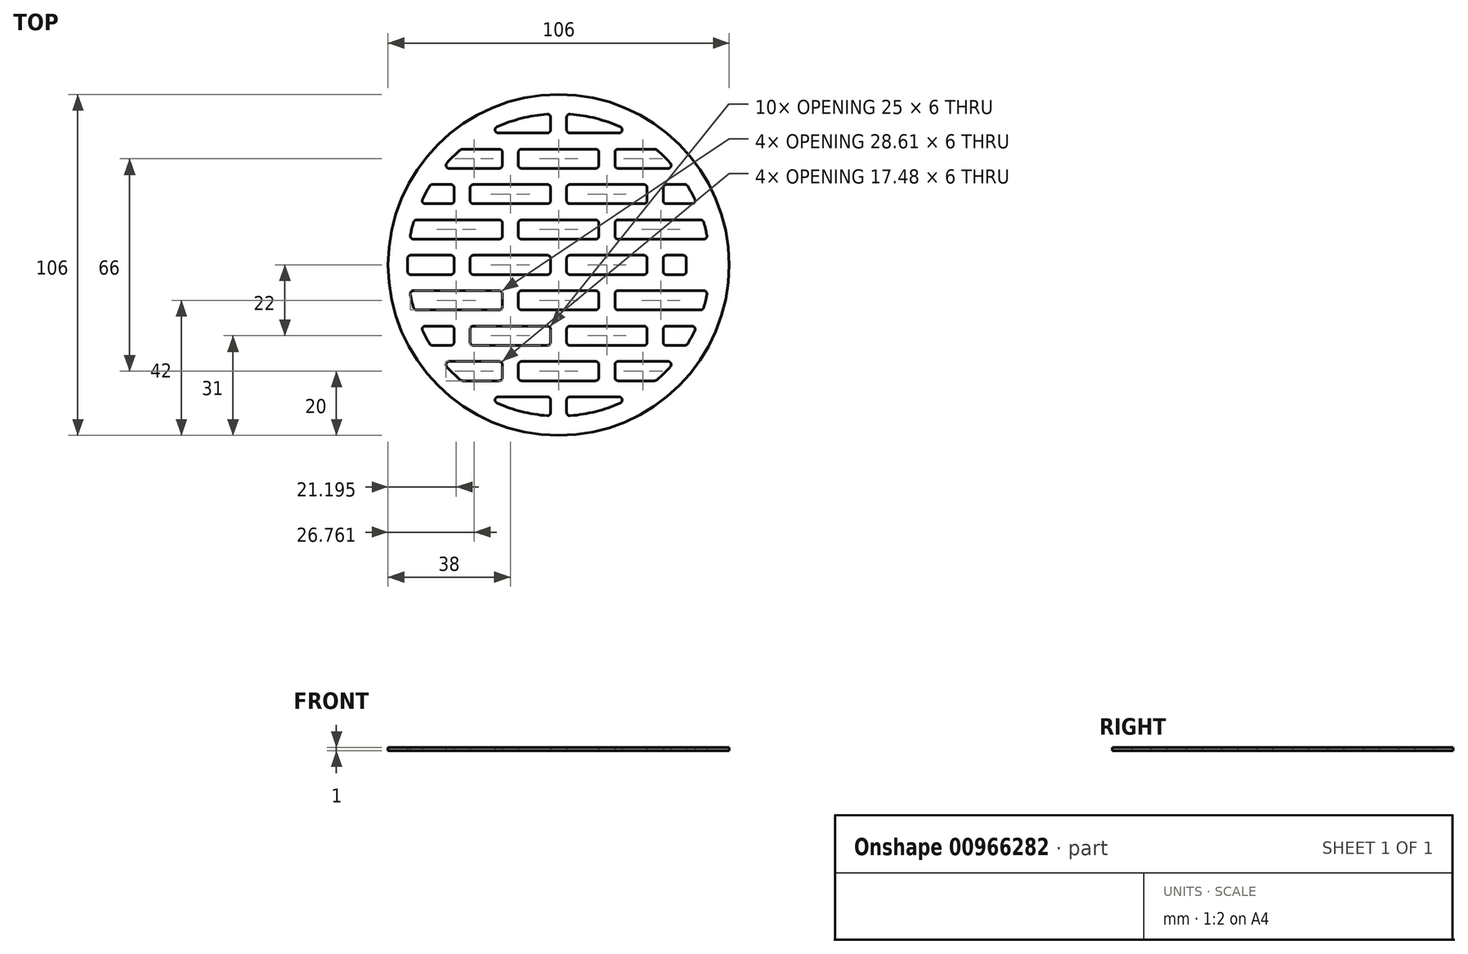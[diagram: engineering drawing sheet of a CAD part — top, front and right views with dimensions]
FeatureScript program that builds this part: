
annotation { "Feature Type Name" : "Feature", "Feature Type Description" : "" }
export const myFeature = defineFeature(function(context is Context, id is Id, definition is map)
    precondition{}
    {
        {
            var Q0;
            Q0=qCreatedBy(makeId("Top.planeOp"),FACE);
            var sketch = newSketch(context, id + "F0", { "sketchPlane" : qUnion([Q0])});
            skCircle(sketch, "E0", {"center": v(0, 0) * mm, "radius": 53 * mm});
            skArc(sketch, "E1", {"start": v(22.98, 41) * mm, "mid": v(13.08, 45.14) * mm, "end": v(2.5, 46.93) * mm});
            skLineSegment(sketch, "E2", {"start": v(-47, 0) * mm, "end": v(39.7, 0) * mm, "construction": true});
            skLineSegment(sketch, "E3.0", {"start": v(-46.9, -3) * mm, "end": v(-32.5, -3) * mm});
            skLineSegment(sketch, "E4.0", {"start": v(-46.9, 3) * mm, "end": v(-32.5, 3) * mm});
            skLineSegment(sketch, "E5", {"start": v(0, 47) * mm, "end": v(0, -47) * mm, "construction": true});
            skLineSegment(sketch, "E6.0", {"start": v(2.5, 46.93) * mm, "end": v(2.5, 41) * mm});
            skLineSegment(sketch, "E7.0", {"start": v(-2.5, 46.93) * mm, "end": v(-2.5, 41) * mm});
            skLineSegment(sketch, "E8.0.1.0", {"start": v(-46.9, 8) * mm, "end": v(-17.5, 8) * mm});
            skLineSegment(sketch, "E8.0.1.1", {"start": v(-44.87, 14) * mm, "end": v(-17.5, 14) * mm});
            skLineSegment(sketch, "E8.0.2.0", {"start": v(-42.99, 19) * mm, "end": v(-32.5, 19) * mm});
            skLineSegment(sketch, "E8.0.2.1", {"start": v(-39.8, 25) * mm, "end": v(-32.5, 25) * mm});
            skLineSegment(sketch, "E8.0.3.0", {"start": v(-36.18, 30) * mm, "end": v(-17.5, 30) * mm});
            skLineSegment(sketch, "E8.direction1", {"start": v(-46.9, -3) * mm, "end": v(-32.5, -3) * mm, "construction": true});
            skLineSegment(sketch, "E8.direction2", {"start": v(-46.9, -3) * mm, "end": v(-46.9, 8) * mm, "construction": true});
            skLineSegment(sketch, "E9.trimOffspring", {"start": v(-27.5, 3) * mm, "end": v(-27.5, -3) * mm});
            skLineSegment(sketch, "E10.trimOffspring", {"start": v(-32.5, 3) * mm, "end": v(-32.5, -3) * mm});
            skLineSegment(sketch, "E11.trimOffspring", {"start": v(-2.5, 3) * mm, "end": v(-2.5, -3) * mm});
            skLineSegment(sketch, "E12.trimOffspring", {"start": v(2.5, 3) * mm, "end": v(2.5, -3) * mm});
            skLineSegment(sketch, "E13.trimOffspring", {"start": v(-12.5, 14) * mm, "end": v(-12.5, 8) * mm});
            skLineSegment(sketch, "E14.trimOffspring", {"start": v(-17.5, 14) * mm, "end": v(-17.5, 8) * mm});
            skLineSegment(sketch, "E15.trimOffspring", {"start": v(2.5, 25) * mm, "end": v(2.5, 19) * mm});
            skLineSegment(sketch, "E16.trimOffspring", {"start": v(-2.5, 25) * mm, "end": v(-2.5, 19) * mm});
            skLineSegment(sketch, "E17.trimOffspring", {"start": v(-27.5, 25) * mm, "end": v(-27.5, 19) * mm});
            skLineSegment(sketch, "E18.trimOffspring", {"start": v(-32.5, 25) * mm, "end": v(-32.5, 19) * mm});
            skLineSegment(sketch, "E19.trimOffspring", {"start": v(-12.5, 36) * mm, "end": v(-12.5, 30) * mm});
            skLineSegment(sketch, "E20.trimOffspring", {"start": v(-17.5, 36) * mm, "end": v(-17.5, 30) * mm});
            skLineSegment(sketch, "E21.trimOffspring", {"start": v(-22.98, 41) * mm, "end": v(-2.5, 41) * mm});
            skLineSegment(sketch, "E22.trimOffspring", {"start": v(-30.22, 36) * mm, "end": v(-17.5, 36) * mm});
            skPoint(sketch, "E23.orphan", {"position": v(-46.9, 30) * mm});
            skPoint(sketch, "E24.orphan", {"position": v(-46.9, 25) * mm});
            skPoint(sketch, "E25.orphan", {"position": v(-46.9, 19) * mm});
            skPoint(sketch, "E26.orphan", {"position": v(-46.9, 14) * mm});
            skPoint(sketch, "E27.orphan", {"position": v(46.9, 8) * mm});
            skPoint(sketch, "E28.orphan", {"position": v(46.9, 14) * mm});
            skPoint(sketch, "E29.orphan", {"position": v(46.9, 19) * mm});
            skPoint(sketch, "E30.orphan", {"position": v(46.9, 25) * mm});
            skPoint(sketch, "E31.orphan", {"position": v(46.9, 30) * mm});
            skPoint(sketch, "E32.orphan", {"position": v(46.9, 41) * mm});
            skArc(sketch, "E33.trimOffspring", {"start": v(-30.22, 36) * mm, "mid": v(-33.33, 33.13) * mm, "end": v(-36.18, 30) * mm});
            skArc(sketch, "E34.trimOffspring", {"start": v(-39.8, 25) * mm, "mid": v(-41.5, 22.06) * mm, "end": v(-42.99, 19) * mm});
            skArc(sketch, "E35.trimOffspring", {"start": v(36.18, 30) * mm, "mid": v(33.33, 33.13) * mm, "end": v(30.22, 36) * mm});
            skArc(sketch, "E36.trimOffspring", {"start": v(42.99, 19) * mm, "mid": v(41.5, 22.06) * mm, "end": v(39.8, 25) * mm});
            skArc(sketch, "E37.trimOffspring", {"start": v(-44.87, 14) * mm, "mid": v(-45.69, 11.02) * mm, "end": v(-46.31, 8) * mm});
            skArc(sketch, "E38.trimOffspring", {"start": v(46.31, 8) * mm, "mid": v(45.69, 11.02) * mm, "end": v(44.87, 14) * mm});
            skArc(sketch, "E39.trimOffspring", {"start": v(-46.9, 3) * mm, "mid": v(-47, 0) * mm, "end": v(-46.9, -3) * mm});
            skLineSegment(sketch, "E40.MirrorCS", {"start": v(27.5, 3) * mm, "end": v(27.5, -3) * mm});
            skLineSegment(sketch, "E41.MirrorCS", {"start": v(32.5, 3) * mm, "end": v(32.5, -3) * mm});
            skLineSegment(sketch, "E42.MirrorCS", {"start": v(17.5, 14) * mm, "end": v(17.5, 8) * mm});
            skLineSegment(sketch, "E43.MirrorCS", {"start": v(12.5, 14) * mm, "end": v(12.5, 8) * mm});
            skLineSegment(sketch, "E44.MirrorCS", {"start": v(27.5, 25) * mm, "end": v(27.5, 19) * mm});
            skLineSegment(sketch, "E45.MirrorCS", {"start": v(32.5, 25) * mm, "end": v(32.5, 19) * mm});
            skLineSegment(sketch, "E46.MirrorCS", {"start": v(12.5, 36) * mm, "end": v(12.5, 30) * mm});
            skLineSegment(sketch, "E47.MirrorCS", {"start": v(17.5, 36) * mm, "end": v(17.5, 30) * mm});
            skLineSegment(sketch, "E48.MirrorCS", {"start": v(-12.5, -36) * mm, "end": v(-12.5, -30) * mm});
            skLineSegment(sketch, "E49.MirrorCS", {"start": v(12.5, -36) * mm, "end": v(12.5, -30) * mm});
            skArc(sketch, "E50.MirrorCS", {"start": v(46.31, -8) * mm, "mid": v(45.69, -11.02) * mm, "end": v(44.87, -14) * mm});
            skArc(sketch, "E51.MirrorCS", {"start": v(-44.87, -14) * mm, "mid": v(-45.69, -11.02) * mm, "end": v(-46.31, -8) * mm});
            skLineSegment(sketch, "E52.MirrorCS", {"start": v(-17.5, -36) * mm, "end": v(-17.5, -30) * mm});
            skLineSegment(sketch, "E53.MirrorCS", {"start": v(17.5, -36) * mm, "end": v(17.5, -30) * mm});
            skLineSegment(sketch, "E54.MirrorCS", {"start": v(-12.5, -14) * mm, "end": v(-12.5, -8) * mm});
            skPoint(sketch, "E55.MirrorP", {"position": v(-46.9, -25) * mm});
            skLineSegment(sketch, "E56.MirrorCS", {"start": v(2.5, -46.93) * mm, "end": v(2.5, -41) * mm});
            skLineSegment(sketch, "E57.MirrorCS", {"start": v(2.5, -25) * mm, "end": v(2.5, -19) * mm});
            skArc(sketch, "E58.MirrorCS", {"start": v(-30.22, -36) * mm, "mid": v(-33.33, -33.13) * mm, "end": v(-36.18, -30) * mm});
            skLineSegment(sketch, "E59.MirrorCS", {"start": v(12.5, -14) * mm, "end": v(12.5, -8) * mm});
            skArc(sketch, "E60.MirrorCS", {"start": v(42.99, -19) * mm, "mid": v(41.5, -22.06) * mm, "end": v(39.8, -25) * mm});
            skPoint(sketch, "E61.MirrorP", {"position": v(46.9, -14) * mm});
            skArc(sketch, "E62.MirrorCS", {"start": v(22.98, -41) * mm, "mid": v(13.08, -45.14) * mm, "end": v(2.5, -46.93) * mm});
            skLineSegment(sketch, "E63.MirrorCS", {"start": v(-44.87, -14) * mm, "end": v(-17.5, -14) * mm});
            skLineSegment(sketch, "E64.MirrorCS", {"start": v(-2.5, -25) * mm, "end": v(-2.5, -19) * mm});
            skLineSegment(sketch, "E65.MirrorCS", {"start": v(32.5, -25) * mm, "end": v(32.5, -19) * mm});
            skLineSegment(sketch, "E66.MirrorCS", {"start": v(17.5, -14) * mm, "end": v(17.5, -8) * mm});
            skPoint(sketch, "E67.MirrorP", {"position": v(-46.9, -30) * mm});
            skLineSegment(sketch, "E68.MirrorCS", {"start": v(-17.5, -14) * mm, "end": v(-17.5, -8) * mm});
            skArc(sketch, "E69.MirrorCS", {"start": v(36.18, -30) * mm, "mid": v(33.33, -33.13) * mm, "end": v(30.22, -36) * mm});
            skPoint(sketch, "E70.MirrorP", {"position": v(-46.9, -19) * mm});
            skLineSegment(sketch, "E71.MirrorCS", {"start": v(-2.5, -46.93) * mm, "end": v(-2.5, -41) * mm});
            skPoint(sketch, "E72.MirrorP", {"position": v(46.9, -41) * mm});
            skPoint(sketch, "E73.MirrorP", {"position": v(46.9, -8) * mm});
            skLineSegment(sketch, "E74.MirrorCS", {"start": v(-46.31, -8) * mm, "end": v(-17.5, -8) * mm});
            skArc(sketch, "E75.MirrorCS", {"start": v(-39.8, -25) * mm, "mid": v(-41.5, -22.06) * mm, "end": v(-42.99, -19) * mm});
            skLineSegment(sketch, "E76.MirrorCS", {"start": v(-32.5, -25) * mm, "end": v(-32.5, -19) * mm});
            skLineSegment(sketch, "E77.MirrorCS", {"start": v(-36.18, -30) * mm, "end": v(-17.5, -30) * mm});
            skPoint(sketch, "E78.MirrorP", {"position": v(-46.9, -14) * mm});
            skLineSegment(sketch, "E79.MirrorCS", {"start": v(-30.22, -36) * mm, "end": v(-17.5, -36) * mm});
            skPoint(sketch, "E80.MirrorP", {"position": v(46.9, -30) * mm});
            skLineSegment(sketch, "E81.MirrorCS", {"start": v(-22.98, -41) * mm, "end": v(-2.5, -41) * mm});
            skLineSegment(sketch, "E82.MirrorCS", {"start": v(-27.5, -25) * mm, "end": v(-27.5, -19) * mm});
            skPoint(sketch, "E83.MirrorP", {"position": v(46.9, -25) * mm});
            skLineSegment(sketch, "E84.MirrorCS", {"start": v(27.5, -25) * mm, "end": v(27.5, -19) * mm});
            skLineSegment(sketch, "E85.MirrorCS", {"start": v(-42.99, -19) * mm, "end": v(-32.5, -19) * mm});
            skLineSegment(sketch, "E86.MirrorCS", {"start": v(-39.8, -25) * mm, "end": v(-32.5, -25) * mm});
            skPoint(sketch, "E87.MirrorP", {"position": v(46.9, -19) * mm});
            skLineSegment(sketch, "E88.trimOffspring", {"start": v(17.5, 36) * mm, "end": v(30.22, 36) * mm});
            skLineSegment(sketch, "E89.trimOffspring", {"start": v(17.5, 30) * mm, "end": v(36.18, 30) * mm});
            skLineSegment(sketch, "E90.trimOffspring", {"start": v(-12.5, 36) * mm, "end": v(12.5, 36) * mm});
            skLineSegment(sketch, "E91.trimOffspring", {"start": v(-12.5, 30) * mm, "end": v(12.5, 30) * mm});
            skLineSegment(sketch, "E92.trimOffspring", {"start": v(-27.5, 25) * mm, "end": v(-2.5, 25) * mm});
            skLineSegment(sketch, "E93.trimOffspring", {"start": v(-27.5, 19) * mm, "end": v(-2.5, 19) * mm});
            skLineSegment(sketch, "E94.trimOffspring", {"start": v(2.5, 25) * mm, "end": v(27.5, 25) * mm});
            skLineSegment(sketch, "E95.trimOffspring", {"start": v(2.5, 19) * mm, "end": v(27.5, 19) * mm});
            skLineSegment(sketch, "E96.trimOffspring", {"start": v(32.5, 25) * mm, "end": v(39.8, 25) * mm});
            skLineSegment(sketch, "E97.trimOffspring", {"start": v(32.5, 19) * mm, "end": v(42.99, 19) * mm});
            skLineSegment(sketch, "E98.trimOffspring", {"start": v(17.5, 14) * mm, "end": v(44.87, 14) * mm});
            skLineSegment(sketch, "E99.trimOffspring", {"start": v(17.5, 8) * mm, "end": v(46.31, 8) * mm});
            skLineSegment(sketch, "E100.trimOffspring", {"start": v(-12.5, 14) * mm, "end": v(12.5, 14) * mm});
            skLineSegment(sketch, "E101.trimOffspring", {"start": v(-12.5, 8) * mm, "end": v(12.5, 8) * mm});
            skLineSegment(sketch, "E102.trimOffspring", {"start": v(-27.5, 3) * mm, "end": v(-2.5, 3) * mm});
            skLineSegment(sketch, "E103.trimOffspring", {"start": v(-27.5, -3) * mm, "end": v(-25.91, -3) * mm, "construction": true});
            skLineSegment(sketch, "E104.trimOffspring", {"start": v(-27.5, -3) * mm, "end": v(-2.5, -3) * mm});
            skLineSegment(sketch, "E105.trimOffspring", {"start": v(2.5, 3) * mm, "end": v(27.5, 3) * mm});
            skLineSegment(sketch, "E106.trimOffspring", {"start": v(2.5, -3) * mm, "end": v(27.5, -3) * mm});
            skLineSegment(sketch, "E107.trimOffspring", {"start": v(32.5, -3) * mm, "end": v(39.7, -3) * mm});
            skLineSegment(sketch, "E108.trimOffspring", {"start": v(32.5, 3) * mm, "end": v(39.7, 3) * mm});
            skLineSegment(sketch, "E109.trimOffspring", {"start": v(17.5, -8) * mm, "end": v(46.31, -8) * mm});
            skLineSegment(sketch, "E110.trimOffspring", {"start": v(17.5, -14) * mm, "end": v(44.87, -14) * mm});
            skLineSegment(sketch, "E111.trimOffspring", {"start": v(-12.5, -8) * mm, "end": v(12.5, -8) * mm});
            skLineSegment(sketch, "E112.trimOffspring", {"start": v(-12.5, -14) * mm, "end": v(12.5, -14) * mm});
            skLineSegment(sketch, "E113.trimOffspring", {"start": v(-27.5, -19) * mm, "end": v(-2.5, -19) * mm});
            skLineSegment(sketch, "E114.trimOffspring", {"start": v(-27.5, -25) * mm, "end": v(-2.5, -25) * mm});
            skLineSegment(sketch, "E115.trimOffspring", {"start": v(2.5, -19) * mm, "end": v(27.5, -19) * mm});
            skLineSegment(sketch, "E116.trimOffspring", {"start": v(2.5, -25) * mm, "end": v(27.5, -25) * mm});
            skLineSegment(sketch, "E117.trimOffspring", {"start": v(32.5, -25) * mm, "end": v(39.8, -25) * mm});
            skLineSegment(sketch, "E118.trimOffspring", {"start": v(32.5, -19) * mm, "end": v(42.99, -19) * mm});
            skLineSegment(sketch, "E119.trimOffspring", {"start": v(17.5, -30) * mm, "end": v(36.18, -30) * mm});
            skLineSegment(sketch, "E120.trimOffspring", {"start": v(17.5, -36) * mm, "end": v(30.22, -36) * mm});
            skLineSegment(sketch, "E121.trimOffspring", {"start": v(-12.5, -30) * mm, "end": v(12.5, -30) * mm});
            skLineSegment(sketch, "E122.trimOffspring", {"start": v(-12.5, -36) * mm, "end": v(12.5, -36) * mm});
            skLineSegment(sketch, "E123.trimOffspring", {"start": v(2.5, -41) * mm, "end": v(22.98, -41) * mm});
            skArc(sketch, "E124.trimOffspring", {"start": v(2.5, -46.93) * mm, "mid": v(13.08, -45.14) * mm, "end": v(22.98, -41) * mm});
            skArc(sketch, "E125.trimOffspring", {"start": v(-2.5, -46.93) * mm, "mid": v(-13.08, -45.14) * mm, "end": v(-22.98, -41) * mm});
            skArc(sketch, "E126.trimOffspring", {"start": v(-2.5, 46.93) * mm, "mid": v(-13.08, 45.14) * mm, "end": v(-22.98, 41) * mm});
            skLineSegment(sketch, "E127.trimOffspring", {"start": v(2.5, 41) * mm, "end": v(22.98, 41) * mm});
            skArc(sketch, "E128.trimOffspring", {"start": v(44.87, -14) * mm, "mid": v(45.69, -11.02) * mm, "end": v(46.31, -8) * mm});
            skArc(sketch, "E129.trimOffspring", {"start": v(39.8, -25) * mm, "mid": v(41.5, -22.06) * mm, "end": v(42.99, -19) * mm});
            skArc(sketch, "E130.trimOffspring", {"start": v(30.22, -36) * mm, "mid": v(33.33, -33.13) * mm, "end": v(36.18, -30) * mm});
            skArc(sketch, "E131.trimOffspring", {"start": v(-22.98, -41) * mm, "mid": v(-13.08, -45.14) * mm, "end": v(-2.5, -46.93) * mm});
            skArc(sketch, "E132.trimOffspring", {"start": v(-36.18, -30) * mm, "mid": v(-33.33, -33.13) * mm, "end": v(-30.22, -36) * mm});
            skArc(sketch, "E133.trimOffspring", {"start": v(-42.99, -19) * mm, "mid": v(-41.5, -22.06) * mm, "end": v(-39.8, -25) * mm});
            skArc(sketch, "E134.trimOffspring", {"start": v(-46.31, -8) * mm, "mid": v(-45.69, -11.02) * mm, "end": v(-44.87, -14) * mm});
            skPoint(sketch, "E135.orphan", {"position": v(-46.9, -8) * mm});
            skLineSegment(sketch, "E136", {"start": v(39.7, 3) * mm, "end": v(39.7, -3) * mm});
            skPoint(sketch, "E137.orphan", {"position": v(46.9, 3) * mm});
            skPoint(sketch, "E138.orphan", {"position": v(46.9, -3) * mm});
            skSolve(sketch);
        }
        {
            var Q0;
            Q0 = qSketchRegion(id + "F0", true);
            extrude(context, id + "F1", {"entities" : qUnion([Q0]), "depth" : 1 * mm, "offsetDistance" : 25 * mm});
        }
        {
            var Q0;
            Q0=makeQuery(id+"F1.opExtrude","SWEPT_EDGE",EDGE,{"disambiguationData":[OSD([sQuery(id+"F0.wireOp",EDGE,"E1"),sQuery(id+"F0.wireOp",EDGE,"E127.trimOffspring")])]});
            var Q1;
            Q1=makeQuery(id+"F1.opExtrude","SWEPT_EDGE",EDGE,{"disambiguationData":[OSD([sQuery(id+"F0.wireOp",EDGE,"E21.trimOffspring"),sQuery(id+"F0.wireOp",EDGE,"E126.trimOffspring")])]});
            var Q2;
            Q2=makeQuery(id+"F1.opExtrude","SWEPT_EDGE",EDGE,{"disambiguationData":[OSD([sQuery(id+"F0.wireOp",EDGE,"E35.trimOffspring"),sQuery(id+"F0.wireOp",EDGE,"E89.trimOffspring")])]});
            var Q3;
            Q3=makeQuery(id+"F1.opExtrude","SWEPT_EDGE",EDGE,{"disambiguationData":[OSD([sQuery(id+"F0.wireOp",EDGE,"E36.trimOffspring"),sQuery(id+"F0.wireOp",EDGE,"E97.trimOffspring")])]});
            var Q4;
            Q4=makeQuery(id+"F1.opExtrude","SWEPT_EDGE",EDGE,{"disambiguationData":[OSD([sQuery(id+"F0.wireOp",EDGE,"E38.trimOffspring"),sQuery(id+"F0.wireOp",EDGE,"E99.trimOffspring")])]});
            var Q5;
            Q5=makeQuery(id+"F1.opExtrude","SWEPT_EDGE",EDGE,{"disambiguationData":[OSD([sQuery(id+"F0.wireOp",EDGE,"E109.trimOffspring"),sQuery(id+"F0.wireOp",EDGE,"E128.trimOffspring")])]});
            var Q6;
            Q6=makeQuery(id+"F1.opExtrude","SWEPT_EDGE",EDGE,{"disambiguationData":[OSD([sQuery(id+"F0.wireOp",EDGE,"E108.trimOffspring"),sQuery(id+"F0.wireOp",EDGE,"af1faaf5-8b60-483f-9866-ba8c8775280e.trimOffspring")])]});
            var Q7;
            Q7=makeQuery(id+"F1.opExtrude","SWEPT_EDGE",EDGE,{"disambiguationData":[OSD([sQuery(id+"F0.wireOp",EDGE,"E107.trimOffspring"),sQuery(id+"F0.wireOp",EDGE,"af1faaf5-8b60-483f-9866-ba8c8775280e.trimOffspring")])]});
            var Q8;
            Q8=makeQuery(id+"F1.opExtrude","SWEPT_EDGE",EDGE,{"disambiguationData":[OSD([sQuery(id+"F0.wireOp",EDGE,"E110.trimOffspring"),sQuery(id+"F0.wireOp",EDGE,"E128.trimOffspring")])]});
            var Q9;
            Q9=makeQuery(id+"F1.opExtrude","SWEPT_EDGE",EDGE,{"disambiguationData":[OSD([sQuery(id+"F0.wireOp",EDGE,"E117.trimOffspring"),sQuery(id+"F0.wireOp",EDGE,"E129.trimOffspring")])]});
            var Q10;
            Q10=makeQuery(id+"F1.opExtrude","SWEPT_EDGE",EDGE,{"disambiguationData":[OSD([sQuery(id+"F0.wireOp",EDGE,"E120.trimOffspring"),sQuery(id+"F0.wireOp",EDGE,"E130.trimOffspring")])]});
            var Q11;
            Q11=makeQuery(id+"F1.opExtrude","SWEPT_EDGE",EDGE,{"disambiguationData":[OSD([sQuery(id+"F0.wireOp",EDGE,"E123.trimOffspring"),sQuery(id+"F0.wireOp",EDGE,"E124.trimOffspring")])]});
            var Q12;
            Q12=makeQuery(id+"F1.opExtrude","SWEPT_EDGE",EDGE,{"disambiguationData":[OSD([sQuery(id+"F0.wireOp",EDGE,"E119.trimOffspring"),sQuery(id+"F0.wireOp",EDGE,"E130.trimOffspring")])]});
            var Q13;
            Q13=makeQuery(id+"F1.opExtrude","SWEPT_EDGE",EDGE,{"disambiguationData":[OSD([sQuery(id+"F0.wireOp",EDGE,"E118.trimOffspring"),sQuery(id+"F0.wireOp",EDGE,"E129.trimOffspring")])]});
            var Q14;
            Q14=makeQuery(id+"F1.opExtrude","SWEPT_EDGE",EDGE,{"disambiguationData":[OSD([sQuery(id+"F0.wireOp",EDGE,"E38.trimOffspring"),sQuery(id+"F0.wireOp",EDGE,"E98.trimOffspring")])]});
            var Q15;
            Q15=makeQuery(id+"F1.opExtrude","SWEPT_EDGE",EDGE,{"disambiguationData":[OSD([sQuery(id+"F0.wireOp",EDGE,"E36.trimOffspring"),sQuery(id+"F0.wireOp",EDGE,"E96.trimOffspring")])]});
            var Q16;
            Q16=makeQuery(id+"F1.opExtrude","SWEPT_EDGE",EDGE,{"disambiguationData":[OSD([sQuery(id+"F0.wireOp",EDGE,"E35.trimOffspring"),sQuery(id+"F0.wireOp",EDGE,"E88.trimOffspring")])]});
            var Q17;
            Q17=makeQuery(id+"F1.opExtrude","SWEPT_EDGE",EDGE,{"disambiguationData":[OSD([sQuery(id+"F0.wireOp",EDGE,"E7.0"),sQuery(id+"F0.wireOp",EDGE,"E126.trimOffspring")])]});
            var Q18;
            Q18=makeQuery(id+"F1.opExtrude","SWEPT_EDGE",EDGE,{"disambiguationData":[OSD([sQuery(id+"F0.wireOp",EDGE,"E7.0"),sQuery(id+"F0.wireOp",EDGE,"E21.trimOffspring")])]});
            var Q19;
            Q19=makeQuery(id+"F1.opExtrude","SWEPT_EDGE",EDGE,{"disambiguationData":[OSD([sQuery(id+"F0.wireOp",EDGE,"E1"),sQuery(id+"F0.wireOp",EDGE,"E6.0")])]});
            var Q20;
            Q20=makeQuery(id+"F1.opExtrude","SWEPT_EDGE",EDGE,{"disambiguationData":[OSD([sQuery(id+"F0.wireOp",EDGE,"E6.0"),sQuery(id+"F0.wireOp",EDGE,"E127.trimOffspring")])]});
            var Q21;
            Q21=makeQuery(id+"F1.opExtrude","SWEPT_EDGE",EDGE,{"disambiguationData":[OSD([sQuery(id+"F0.wireOp",EDGE,"E8.0.3.0"),sQuery(id+"F0.wireOp",EDGE,"E33.trimOffspring")])]});
            var Q22;
            Q22=makeQuery(id+"F1.opExtrude","SWEPT_EDGE",EDGE,{"disambiguationData":[OSD([sQuery(id+"F0.wireOp",EDGE,"E22.trimOffspring"),sQuery(id+"F0.wireOp",EDGE,"E33.trimOffspring")])]});
            var Q23;
            Q23=makeQuery(id+"F1.opExtrude","SWEPT_EDGE",EDGE,{"disambiguationData":[OSD([sQuery(id+"F0.wireOp",EDGE,"E20.trimOffspring"),sQuery(id+"F0.wireOp",EDGE,"E22.trimOffspring")])]});
            var Q24;
            Q24=makeQuery(id+"F1.opExtrude","SWEPT_EDGE",EDGE,{"disambiguationData":[OSD([sQuery(id+"F0.wireOp",EDGE,"E8.0.3.0"),sQuery(id+"F0.wireOp",EDGE,"E20.trimOffspring")])]});
            var Q25;
            Q25=makeQuery(id+"F1.opExtrude","SWEPT_EDGE",EDGE,{"disambiguationData":[OSD([sQuery(id+"F0.wireOp",EDGE,"E16.trimOffspring"),sQuery(id+"F0.wireOp",EDGE,"E93.trimOffspring")])]});
            var Q26;
            Q26=makeQuery(id+"F1.opExtrude","SWEPT_EDGE",EDGE,{"disambiguationData":[OSD([sQuery(id+"F0.wireOp",EDGE,"E8.0.2.0"),sQuery(id+"F0.wireOp",EDGE,"E18.trimOffspring")])]});
            var Q27;
            Q27=makeQuery(id+"F1.opExtrude","SWEPT_EDGE",EDGE,{"disambiguationData":[OSD([sQuery(id+"F0.wireOp",EDGE,"E8.0.2.1"),sQuery(id+"F0.wireOp",EDGE,"E18.trimOffspring")])]});
            var Q28;
            Q28=makeQuery(id+"F1.opExtrude","SWEPT_EDGE",EDGE,{"disambiguationData":[OSD([sQuery(id+"F0.wireOp",EDGE,"E8.0.2.1"),sQuery(id+"F0.wireOp",EDGE,"E34.trimOffspring")])]});
            var Q29;
            Q29=makeQuery(id+"F1.opExtrude","SWEPT_EDGE",EDGE,{"disambiguationData":[OSD([sQuery(id+"F0.wireOp",EDGE,"E8.0.2.0"),sQuery(id+"F0.wireOp",EDGE,"E34.trimOffspring")])]});
            var Q30;
            Q30=makeQuery(id+"F1.opExtrude","SWEPT_EDGE",EDGE,{"disambiguationData":[OSD([sQuery(id+"F0.wireOp",EDGE,"E17.trimOffspring"),sQuery(id+"F0.wireOp",EDGE,"E93.trimOffspring")])]});
            var Q31;
            Q31=makeQuery(id+"F1.opExtrude","SWEPT_EDGE",EDGE,{"disambiguationData":[OSD([sQuery(id+"F0.wireOp",EDGE,"E17.trimOffspring"),sQuery(id+"F0.wireOp",EDGE,"E92.trimOffspring")])]});
            var Q32;
            Q32=makeQuery(id+"F1.opExtrude","SWEPT_EDGE",EDGE,{"disambiguationData":[OSD([sQuery(id+"F0.wireOp",EDGE,"E16.trimOffspring"),sQuery(id+"F0.wireOp",EDGE,"E92.trimOffspring")])]});
            var Q33;
            Q33=makeQuery(id+"F1.opExtrude","SWEPT_EDGE",EDGE,{"disambiguationData":[OSD([sQuery(id+"F0.wireOp",EDGE,"E46.MirrorCS"),sQuery(id+"F0.wireOp",EDGE,"E90.trimOffspring")])]});
            var Q34;
            Q34=makeQuery(id+"F1.opExtrude","SWEPT_EDGE",EDGE,{"disambiguationData":[OSD([sQuery(id+"F0.wireOp",EDGE,"E19.trimOffspring"),sQuery(id+"F0.wireOp",EDGE,"E90.trimOffspring")])]});
            var Q35;
            Q35=makeQuery(id+"F1.opExtrude","SWEPT_EDGE",EDGE,{"disambiguationData":[OSD([sQuery(id+"F0.wireOp",EDGE,"E19.trimOffspring"),sQuery(id+"F0.wireOp",EDGE,"E91.trimOffspring")])]});
            var Q36;
            Q36=makeQuery(id+"F1.opExtrude","SWEPT_EDGE",EDGE,{"disambiguationData":[OSD([sQuery(id+"F0.wireOp",EDGE,"E46.MirrorCS"),sQuery(id+"F0.wireOp",EDGE,"E91.trimOffspring")])]});
            var Q37;
            Q37=makeQuery(id+"F1.opExtrude","SWEPT_EDGE",EDGE,{"disambiguationData":[OSD([sQuery(id+"F0.wireOp",EDGE,"E47.MirrorCS"),sQuery(id+"F0.wireOp",EDGE,"E89.trimOffspring")])]});
            var Q38;
            Q38=makeQuery(id+"F1.opExtrude","SWEPT_EDGE",EDGE,{"disambiguationData":[OSD([sQuery(id+"F0.wireOp",EDGE,"E47.MirrorCS"),sQuery(id+"F0.wireOp",EDGE,"E88.trimOffspring")])]});
            var Q39;
            Q39=makeQuery(id+"F1.opExtrude","SWEPT_EDGE",EDGE,{"disambiguationData":[OSD([sQuery(id+"F0.wireOp",EDGE,"E45.MirrorCS"),sQuery(id+"F0.wireOp",EDGE,"E96.trimOffspring")])]});
            var Q40;
            Q40=makeQuery(id+"F1.opExtrude","SWEPT_EDGE",EDGE,{"disambiguationData":[OSD([sQuery(id+"F0.wireOp",EDGE,"E45.MirrorCS"),sQuery(id+"F0.wireOp",EDGE,"E97.trimOffspring")])]});
            var Q41;
            Q41=makeQuery(id+"F1.opExtrude","SWEPT_EDGE",EDGE,{"disambiguationData":[OSD([sQuery(id+"F0.wireOp",EDGE,"E44.MirrorCS"),sQuery(id+"F0.wireOp",EDGE,"E95.trimOffspring")])]});
            var Q42;
            Q42=makeQuery(id+"F1.opExtrude","SWEPT_EDGE",EDGE,{"disambiguationData":[OSD([sQuery(id+"F0.wireOp",EDGE,"E44.MirrorCS"),sQuery(id+"F0.wireOp",EDGE,"E94.trimOffspring")])]});
            var Q43;
            Q43=makeQuery(id+"F1.opExtrude","SWEPT_EDGE",EDGE,{"disambiguationData":[OSD([sQuery(id+"F0.wireOp",EDGE,"E15.trimOffspring"),sQuery(id+"F0.wireOp",EDGE,"E94.trimOffspring")])]});
            var Q44;
            Q44=makeQuery(id+"F1.opExtrude","SWEPT_EDGE",EDGE,{"disambiguationData":[OSD([sQuery(id+"F0.wireOp",EDGE,"E15.trimOffspring"),sQuery(id+"F0.wireOp",EDGE,"E95.trimOffspring")])]});
            var Q45;
            Q45=makeQuery(id+"F1.opExtrude","SWEPT_EDGE",EDGE,{"disambiguationData":[OSD([sQuery(id+"F0.wireOp",EDGE,"E42.MirrorCS"),sQuery(id+"F0.wireOp",EDGE,"E98.trimOffspring")])]});
            var Q46;
            Q46=makeQuery(id+"F1.opExtrude","SWEPT_EDGE",EDGE,{"disambiguationData":[OSD([sQuery(id+"F0.wireOp",EDGE,"E42.MirrorCS"),sQuery(id+"F0.wireOp",EDGE,"E99.trimOffspring")])]});
            var Q47;
            Q47=makeQuery(id+"F1.opExtrude","SWEPT_EDGE",EDGE,{"disambiguationData":[OSD([sQuery(id+"F0.wireOp",EDGE,"E13.trimOffspring"),sQuery(id+"F0.wireOp",EDGE,"E101.trimOffspring")])]});
            var Q48;
            Q48=makeQuery(id+"F1.opExtrude","SWEPT_EDGE",EDGE,{"disambiguationData":[OSD([sQuery(id+"F0.wireOp",EDGE,"E8.0.1.0"),sQuery(id+"F0.wireOp",EDGE,"E37.trimOffspring")])]});
            var Q49;
            Q49=makeQuery(id+"F1.opExtrude","SWEPT_EDGE",EDGE,{"disambiguationData":[OSD([sQuery(id+"F0.wireOp",EDGE,"E13.trimOffspring"),sQuery(id+"F0.wireOp",EDGE,"E100.trimOffspring")])]});
            var Q50;
            Q50=makeQuery(id+"F1.opExtrude","SWEPT_EDGE",EDGE,{"disambiguationData":[OSD([sQuery(id+"F0.wireOp",EDGE,"E8.0.1.1"),sQuery(id+"F0.wireOp",EDGE,"E37.trimOffspring")])]});
            var Q51;
            Q51=makeQuery(id+"F1.opExtrude","SWEPT_EDGE",EDGE,{"disambiguationData":[OSD([sQuery(id+"F0.wireOp",EDGE,"E8.0.1.1"),sQuery(id+"F0.wireOp",EDGE,"E14.trimOffspring")])]});
            var Q52;
            Q52=makeQuery(id+"F1.opExtrude","SWEPT_EDGE",EDGE,{"disambiguationData":[OSD([sQuery(id+"F0.wireOp",EDGE,"E8.0.1.0"),sQuery(id+"F0.wireOp",EDGE,"E14.trimOffspring")])]});
            var Q53;
            Q53=makeQuery(id+"F1.opExtrude","SWEPT_EDGE",EDGE,{"disambiguationData":[OSD([sQuery(id+"F0.wireOp",EDGE,"E43.MirrorCS"),sQuery(id+"F0.wireOp",EDGE,"E101.trimOffspring")])]});
            var Q54;
            Q54=makeQuery(id+"F1.opExtrude","SWEPT_EDGE",EDGE,{"disambiguationData":[OSD([sQuery(id+"F0.wireOp",EDGE,"E43.MirrorCS"),sQuery(id+"F0.wireOp",EDGE,"E100.trimOffspring")])]});
            var Q55;
            Q55=makeQuery(id+"F1.opExtrude","SWEPT_EDGE",EDGE,{"disambiguationData":[OSD([sQuery(id+"F0.wireOp",EDGE,"E40.MirrorCS"),sQuery(id+"F0.wireOp",EDGE,"E105.trimOffspring")])]});
            var Q56;
            Q56=makeQuery(id+"F1.opExtrude","SWEPT_EDGE",EDGE,{"disambiguationData":[OSD([sQuery(id+"F0.wireOp",EDGE,"E40.MirrorCS"),sQuery(id+"F0.wireOp",EDGE,"E106.trimOffspring")])]});
            var Q57;
            Q57=makeQuery(id+"F1.opExtrude","SWEPT_EDGE",EDGE,{"disambiguationData":[OSD([sQuery(id+"F0.wireOp",EDGE,"E11.trimOffspring"),sQuery(id+"F0.wireOp",EDGE,"E104.trimOffspring")])]});
            var Q58;
            Q58=makeQuery(id+"F1.opExtrude","SWEPT_EDGE",EDGE,{"disambiguationData":[OSD([sQuery(id+"F0.wireOp",EDGE,"E11.trimOffspring"),sQuery(id+"F0.wireOp",EDGE,"E102.trimOffspring")])]});
            var Q59;
            Q59=makeQuery(id+"F1.opExtrude","SWEPT_EDGE",EDGE,{"disambiguationData":[OSD([sQuery(id+"F0.wireOp",EDGE,"E4.0"),sQuery(id+"F0.wireOp",EDGE,"E10.trimOffspring")])]});
            var Q60;
            Q60=makeQuery(id+"F1.opExtrude","SWEPT_EDGE",EDGE,{"disambiguationData":[OSD([sQuery(id+"F0.wireOp",EDGE,"E3.0"),sQuery(id+"F0.wireOp",EDGE,"E10.trimOffspring")])]});
            var Q61;
            Q61=makeQuery(id+"F1.opExtrude","SWEPT_EDGE",EDGE,{"disambiguationData":[OSD([sQuery(id+"F0.wireOp",EDGE,"E4.0"),sQuery(id+"F0.wireOp",EDGE,"E39.trimOffspring")])]});
            var Q62;
            Q62=makeQuery(id+"F1.opExtrude","SWEPT_EDGE",EDGE,{"disambiguationData":[OSD([sQuery(id+"F0.wireOp",EDGE,"E63.MirrorCS"),sQuery(id+"F0.wireOp",EDGE,"E134.trimOffspring")])]});
            var Q63;
            Q63=makeQuery(id+"F1.opExtrude","SWEPT_EDGE",EDGE,{"disambiguationData":[OSD([sQuery(id+"F0.wireOp",EDGE,"E3.0"),sQuery(id+"F0.wireOp",EDGE,"E39.trimOffspring")])]});
            var Q64;
            Q64=makeQuery(id+"F1.opExtrude","SWEPT_EDGE",EDGE,{"disambiguationData":[OSD([sQuery(id+"F0.wireOp",EDGE,"E9.trimOffspring"),sQuery(id+"F0.wireOp",EDGE,"E104.trimOffspring")])]});
            var Q65;
            Q65=makeQuery(id+"F1.opExtrude","SWEPT_EDGE",EDGE,{"disambiguationData":[OSD([sQuery(id+"F0.wireOp",EDGE,"E12.trimOffspring"),sQuery(id+"F0.wireOp",EDGE,"E106.trimOffspring")])]});
            var Q66;
            Q66=makeQuery(id+"F1.opExtrude","SWEPT_EDGE",EDGE,{"disambiguationData":[OSD([sQuery(id+"F0.wireOp",EDGE,"E12.trimOffspring"),sQuery(id+"F0.wireOp",EDGE,"E105.trimOffspring")])]});
            var Q67;
            Q67=makeQuery(id+"F1.opExtrude","SWEPT_EDGE",EDGE,{"disambiguationData":[OSD([sQuery(id+"F0.wireOp",EDGE,"E68.MirrorCS"),sQuery(id+"F0.wireOp",EDGE,"E74.MirrorCS")])]});
            var Q68;
            Q68=makeQuery(id+"F1.opExtrude","SWEPT_EDGE",EDGE,{"disambiguationData":[OSD([sQuery(id+"F0.wireOp",EDGE,"E63.MirrorCS"),sQuery(id+"F0.wireOp",EDGE,"E68.MirrorCS")])]});
            var Q69;
            Q69=makeQuery(id+"F1.opExtrude","SWEPT_EDGE",EDGE,{"disambiguationData":[OSD([sQuery(id+"F0.wireOp",EDGE,"E74.MirrorCS"),sQuery(id+"F0.wireOp",EDGE,"E134.trimOffspring")])]});
            var Q70;
            Q70=makeQuery(id+"F1.opExtrude","SWEPT_EDGE",EDGE,{"disambiguationData":[OSD([sQuery(id+"F0.wireOp",EDGE,"E54.MirrorCS"),sQuery(id+"F0.wireOp",EDGE,"E111.trimOffspring")])]});
            var Q71;
            Q71=makeQuery(id+"F1.opExtrude","SWEPT_EDGE",EDGE,{"disambiguationData":[OSD([sQuery(id+"F0.wireOp",EDGE,"E54.MirrorCS"),sQuery(id+"F0.wireOp",EDGE,"E112.trimOffspring")])]});
            var Q72;
            Q72=makeQuery(id+"F1.opExtrude","SWEPT_EDGE",EDGE,{"disambiguationData":[OSD([sQuery(id+"F0.wireOp",EDGE,"E59.MirrorCS"),sQuery(id+"F0.wireOp",EDGE,"E112.trimOffspring")])]});
            var Q73;
            Q73=makeQuery(id+"F1.opExtrude","SWEPT_EDGE",EDGE,{"disambiguationData":[OSD([sQuery(id+"F0.wireOp",EDGE,"E59.MirrorCS"),sQuery(id+"F0.wireOp",EDGE,"E111.trimOffspring")])]});
            var Q74;
            Q74=makeQuery(id+"F1.opExtrude","SWEPT_EDGE",EDGE,{"disambiguationData":[OSD([sQuery(id+"F0.wireOp",EDGE,"E66.MirrorCS"),sQuery(id+"F0.wireOp",EDGE,"E109.trimOffspring")])]});
            var Q75;
            Q75=makeQuery(id+"F1.opExtrude","SWEPT_EDGE",EDGE,{"disambiguationData":[OSD([sQuery(id+"F0.wireOp",EDGE,"E66.MirrorCS"),sQuery(id+"F0.wireOp",EDGE,"E110.trimOffspring")])]});
            var Q76;
            Q76=makeQuery(id+"F1.opExtrude","SWEPT_EDGE",EDGE,{"disambiguationData":[OSD([sQuery(id+"F0.wireOp",EDGE,"E65.MirrorCS"),sQuery(id+"F0.wireOp",EDGE,"E118.trimOffspring")])]});
            var Q77;
            Q77=makeQuery(id+"F1.opExtrude","SWEPT_EDGE",EDGE,{"disambiguationData":[OSD([sQuery(id+"F0.wireOp",EDGE,"E65.MirrorCS"),sQuery(id+"F0.wireOp",EDGE,"E117.trimOffspring")])]});
            var Q78;
            Q78=makeQuery(id+"F1.opExtrude","SWEPT_EDGE",EDGE,{"disambiguationData":[OSD([sQuery(id+"F0.wireOp",EDGE,"E53.MirrorCS"),sQuery(id+"F0.wireOp",EDGE,"E120.trimOffspring")])]});
            var Q79;
            Q79=makeQuery(id+"F1.opExtrude","SWEPT_EDGE",EDGE,{"disambiguationData":[OSD([sQuery(id+"F0.wireOp",EDGE,"E53.MirrorCS"),sQuery(id+"F0.wireOp",EDGE,"E119.trimOffspring")])]});
            var Q80;
            Q80=makeQuery(id+"F1.opExtrude","SWEPT_EDGE",EDGE,{"disambiguationData":[OSD([sQuery(id+"F0.wireOp",EDGE,"E57.MirrorCS"),sQuery(id+"F0.wireOp",EDGE,"E115.trimOffspring")])]});
            var Q81;
            Q81=makeQuery(id+"F1.opExtrude","SWEPT_EDGE",EDGE,{"disambiguationData":[OSD([sQuery(id+"F0.wireOp",EDGE,"E84.MirrorCS"),sQuery(id+"F0.wireOp",EDGE,"E115.trimOffspring")])]});
            var Q82;
            Q82=makeQuery(id+"F1.opExtrude","SWEPT_EDGE",EDGE,{"disambiguationData":[OSD([sQuery(id+"F0.wireOp",EDGE,"E84.MirrorCS"),sQuery(id+"F0.wireOp",EDGE,"E116.trimOffspring")])]});
            var Q83;
            Q83=makeQuery(id+"F1.opExtrude","SWEPT_EDGE",EDGE,{"disambiguationData":[OSD([sQuery(id+"F0.wireOp",EDGE,"E57.MirrorCS"),sQuery(id+"F0.wireOp",EDGE,"E116.trimOffspring")])]});
            var Q84;
            Q84=makeQuery(id+"F1.opExtrude","SWEPT_EDGE",EDGE,{"disambiguationData":[OSD([sQuery(id+"F0.wireOp",EDGE,"E48.MirrorCS"),sQuery(id+"F0.wireOp",EDGE,"E122.trimOffspring")])]});
            var Q85;
            Q85=makeQuery(id+"F1.opExtrude","SWEPT_EDGE",EDGE,{"disambiguationData":[OSD([sQuery(id+"F0.wireOp",EDGE,"E79.MirrorCS"),sQuery(id+"F0.wireOp",EDGE,"E132.trimOffspring")])]});
            var Q86;
            Q86=makeQuery(id+"F1.opExtrude","SWEPT_EDGE",EDGE,{"disambiguationData":[OSD([sQuery(id+"F0.wireOp",EDGE,"E77.MirrorCS"),sQuery(id+"F0.wireOp",EDGE,"E132.trimOffspring")])]});
            var Q87;
            Q87=makeQuery(id+"F1.opExtrude","SWEPT_EDGE",EDGE,{"disambiguationData":[OSD([sQuery(id+"F0.wireOp",EDGE,"E52.MirrorCS"),sQuery(id+"F0.wireOp",EDGE,"E77.MirrorCS")])]});
            var Q88;
            Q88=makeQuery(id+"F1.opExtrude","SWEPT_EDGE",EDGE,{"disambiguationData":[OSD([sQuery(id+"F0.wireOp",EDGE,"E52.MirrorCS"),sQuery(id+"F0.wireOp",EDGE,"E79.MirrorCS")])]});
            var Q89;
            Q89=makeQuery(id+"F1.opExtrude","SWEPT_EDGE",EDGE,{"disambiguationData":[OSD([sQuery(id+"F0.wireOp",EDGE,"E71.MirrorCS"),sQuery(id+"F0.wireOp",EDGE,"E131.trimOffspring")])]});
            var Q90;
            Q90=makeQuery(id+"F1.opExtrude","SWEPT_EDGE",EDGE,{"disambiguationData":[OSD([sQuery(id+"F0.wireOp",EDGE,"E81.MirrorCS"),sQuery(id+"F0.wireOp",EDGE,"E131.trimOffspring")])]});
            var Q91;
            Q91=makeQuery(id+"F1.opExtrude","SWEPT_EDGE",EDGE,{"disambiguationData":[OSD([sQuery(id+"F0.wireOp",EDGE,"E71.MirrorCS"),sQuery(id+"F0.wireOp",EDGE,"E81.MirrorCS")])]});
            var Q92;
            Q92=makeQuery(id+"F1.opExtrude","SWEPT_EDGE",EDGE,{"disambiguationData":[OSD([sQuery(id+"F0.wireOp",EDGE,"E56.MirrorCS"),sQuery(id+"F0.wireOp",EDGE,"E123.trimOffspring")])]});
            var Q93;
            Q93=makeQuery(id+"F1.opExtrude","SWEPT_EDGE",EDGE,{"disambiguationData":[OSD([sQuery(id+"F0.wireOp",EDGE,"E56.MirrorCS"),sQuery(id+"F0.wireOp",EDGE,"E124.trimOffspring")])]});
            var Q94;
            Q94=makeQuery(id+"F1.opExtrude","SWEPT_EDGE",EDGE,{"disambiguationData":[OSD([sQuery(id+"F0.wireOp",EDGE,"E48.MirrorCS"),sQuery(id+"F0.wireOp",EDGE,"E121.trimOffspring")])]});
            var Q95;
            Q95=makeQuery(id+"F1.opExtrude","SWEPT_EDGE",EDGE,{"disambiguationData":[OSD([sQuery(id+"F0.wireOp",EDGE,"E49.MirrorCS"),sQuery(id+"F0.wireOp",EDGE,"E122.trimOffspring")])]});
            var Q96;
            Q96=makeQuery(id+"F1.opExtrude","SWEPT_EDGE",EDGE,{"disambiguationData":[OSD([sQuery(id+"F0.wireOp",EDGE,"E49.MirrorCS"),sQuery(id+"F0.wireOp",EDGE,"E121.trimOffspring")])]});
            var Q97;
            Q97=makeQuery(id+"F1.opExtrude","SWEPT_EDGE",EDGE,{"disambiguationData":[OSD([sQuery(id+"F0.wireOp",EDGE,"E64.MirrorCS"),sQuery(id+"F0.wireOp",EDGE,"E113.trimOffspring")])]});
            var Q98;
            Q98=makeQuery(id+"F1.opExtrude","SWEPT_EDGE",EDGE,{"disambiguationData":[OSD([sQuery(id+"F0.wireOp",EDGE,"E76.MirrorCS"),sQuery(id+"F0.wireOp",EDGE,"E85.MirrorCS")])]});
            var Q99;
            Q99=makeQuery(id+"F1.opExtrude","SWEPT_EDGE",EDGE,{"disambiguationData":[OSD([sQuery(id+"F0.wireOp",EDGE,"E85.MirrorCS"),sQuery(id+"F0.wireOp",EDGE,"E133.trimOffspring")])]});
            var Q100;
            Q100=makeQuery(id+"F1.opExtrude","SWEPT_EDGE",EDGE,{"disambiguationData":[OSD([sQuery(id+"F0.wireOp",EDGE,"E82.MirrorCS"),sQuery(id+"F0.wireOp",EDGE,"E113.trimOffspring")])]});
            var Q101;
            Q101=makeQuery(id+"F1.opExtrude","SWEPT_EDGE",EDGE,{"disambiguationData":[OSD([sQuery(id+"F0.wireOp",EDGE,"E86.MirrorCS"),sQuery(id+"F0.wireOp",EDGE,"E133.trimOffspring")])]});
            var Q102;
            Q102=makeQuery(id+"F1.opExtrude","SWEPT_EDGE",EDGE,{"disambiguationData":[OSD([sQuery(id+"F0.wireOp",EDGE,"E82.MirrorCS"),sQuery(id+"F0.wireOp",EDGE,"E114.trimOffspring")])]});
            var Q103;
            Q103=makeQuery(id+"F1.opExtrude","SWEPT_EDGE",EDGE,{"disambiguationData":[OSD([sQuery(id+"F0.wireOp",EDGE,"E76.MirrorCS"),sQuery(id+"F0.wireOp",EDGE,"E86.MirrorCS")])]});
            var Q104;
            Q104=makeQuery(id+"F1.opExtrude","SWEPT_EDGE",EDGE,{"disambiguationData":[OSD([sQuery(id+"F0.wireOp",EDGE,"E64.MirrorCS"),sQuery(id+"F0.wireOp",EDGE,"E114.trimOffspring")])]});
            var Q105;
            Q105=makeQuery(id+"F1.opExtrude","SWEPT_EDGE",EDGE,{"disambiguationData":[OSD([sQuery(id+"F0.wireOp",EDGE,"E9.trimOffspring"),sQuery(id+"F0.wireOp",EDGE,"E102.trimOffspring")])]});
            fillet(context, id + "F2", {"entities" : qUnion([Q0, Q1, Q2, Q3, Q4, Q5, Q6, Q7, Q8, Q9, Q10, Q11, Q12, Q13, Q14, Q15, Q16, Q17, Q18, Q19, Q20, Q21, Q22, Q23, Q24, Q25, Q26, Q27, Q28, Q29, Q30, Q31, Q32, Q33, Q34, Q35, Q36, Q37, Q38, Q39, Q40, Q41, Q42, Q43, Q44, Q45, Q46, Q47, Q48, Q49, Q50, Q51, Q52, Q53, Q54, Q55, Q56, Q57, Q58, Q59, Q60, Q61, Q62, Q63, Q64, Q65, Q66, Q67, Q68, Q69, Q70, Q71, Q72, Q73, Q74, Q75, Q76, Q77, Q78, Q79, Q80, Q81, Q82, Q83, Q84, Q85, Q86, Q87, Q88, Q89, Q90, Q91, Q92, Q93, Q94, Q95, Q96, Q97, Q98, Q99, Q100, Q101, Q102, Q103, Q104, Q105]), "radius" : 1 * mm, "tangentPropagation" : true, "allowEdgeOverflow" : false});
        }
    });
